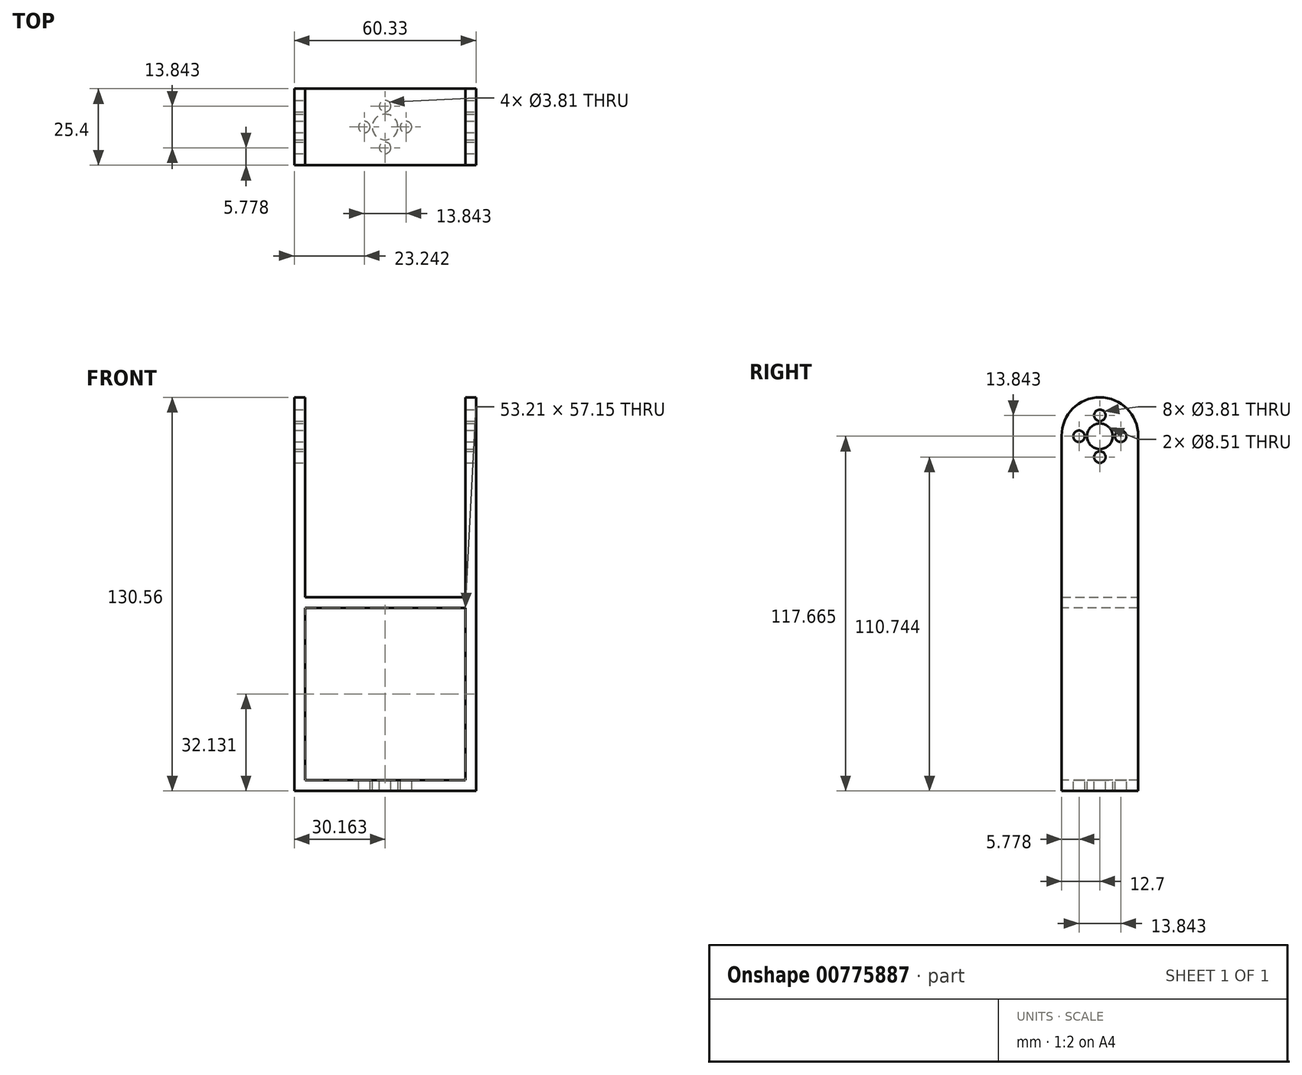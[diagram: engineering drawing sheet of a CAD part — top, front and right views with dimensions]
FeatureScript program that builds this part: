
annotation { "Feature Type Name" : "Feature", "Feature Type Description" : "" }
export const myFeature = defineFeature(function(context is Context, id is Id, definition is map)
    precondition{}
    {
        {
            var Q0;
            Q0=qCreatedBy(makeId("Top.planeOp"),FACE);
            var sketch = newSketch(context, id + "F0", { "sketchPlane" : qUnion([Q0])});
            skLineSegment(sketch, "E0.bottom", {"start": v(-26.29, 12.7) * mm, "end": v(34.04, 12.7) * mm});
            skLineSegment(sketch, "E0.top", {"start": v(-26.29, -12.7) * mm, "end": v(34.04, -12.7) * mm});
            skLineSegment(sketch, "E0.left", {"start": v(-26.29, 12.7) * mm, "end": v(-26.29, -12.7) * mm});
            skLineSegment(sketch, "E0.right", {"start": v(34.04, 12.7) * mm, "end": v(34.04, -12.7) * mm});
            skSolve(sketch);
        }
        {
            var Q0;
            Q0=makeQuery(id+"F0.imprint","IMPRINT",FACE,{"disambiguationData":[TD([[makeQuery(id+"F0.imprint","IMPRINT",EDGE,{"derivedFrom":sQuery(id+"F0.wireOp",EDGE,"E0.bottom")}),-1.0]])]});
            extrude(context, id + "F1", {"entities" : qUnion([Q0]), "depth" : 3.56 * mm});
        }
        {
            var Q0;
            Q0=makeQuery(id+"F1.opExtrude","CAP_FACE",FACE,{"disambiguationData":[OSD([sQuery(id+"F0.wireOp",EDGE,"E0.bottom"),sQuery(id+"F0.wireOp",EDGE,"E0.top"),sQuery(id+"F0.wireOp",EDGE,"E0.left"),sQuery(id+"F0.wireOp",EDGE,"E0.right")])],"isStart":false});
            var sketch = newSketch(context, id + "F2", { "sketchPlane" : qUnion([Q0])});
            skLineSegment(sketch, "E1.bottom", {"start": v(-26.29, 12.7) * mm, "end": v(-22.73, 12.7) * mm});
            skLineSegment(sketch, "E1.top", {"start": v(-26.29, -12.7) * mm, "end": v(-22.73, -12.7) * mm});
            skLineSegment(sketch, "E1.left", {"start": v(-26.29, 12.7) * mm, "end": v(-26.29, -12.7) * mm});
            skLineSegment(sketch, "E1.right", {"start": v(-22.73, 12.7) * mm, "end": v(-22.73, -12.7) * mm});
            skLineSegment(sketch, "E2.bottom", {"start": v(34.04, 12.7) * mm, "end": v(30.48, 12.7) * mm});
            skLineSegment(sketch, "E2.top", {"start": v(34.04, -12.7) * mm, "end": v(30.48, -12.7) * mm});
            skLineSegment(sketch, "E2.left", {"start": v(34.04, 12.7) * mm, "end": v(34.04, -12.7) * mm});
            skLineSegment(sketch, "E2.right", {"start": v(30.48, 12.7) * mm, "end": v(30.48, -12.7) * mm});
            skSolve(sketch);
        }
        {
            var Q0;
            Q0=makeQuery(id+"F2.imprint","IMPRINT",FACE,{"disambiguationData":[TD([[makeQuery(id+"F2.imprint","IMPRINT",EDGE,{"derivedFrom":sQuery(id+"F2.wireOp",EDGE,"E1.bottom")}),-1.0]])]});
            var Q1;
            Q1=makeQuery(id+"F2.imprint","IMPRINT",FACE,{"disambiguationData":[TD([[makeQuery(id+"F2.imprint","IMPRINT",EDGE,{"derivedFrom":sQuery(id+"F2.wireOp",EDGE,"E2.bottom")}),-1.0]])]});
            extrude(context, id + "F3", {"entities" : qUnion([Q0, Q1]), "operationType" : NewBodyOperationType.ADD, "depth" : 127 * mm});
        }
        {
            var Q0;
            Q0=makeQuery(id+"F3.opExtrude","CAP_EDGE",EDGE,{"disambiguationData":[OSD([sQuery(id+"F2.wireOp",EDGE,"E2.bottom")])],"isStart":false});
            fillet(context, id + "F4", {"entities" : qUnion([Q0]), "radius" : 12.7 * mm, "tangentPropagation" : true, "allowEdgeOverflow" : false});
        }
        {
            var Q0;
            Q0=makeQuery(id+"F3.opExtrude","CAP_EDGE",EDGE,{"disambiguationData":[OSD([sQuery(id+"F2.wireOp",EDGE,"E2.top")])],"isStart":false});
            var Q1;
            Q1=makeQuery(id+"F3.opExtrude","CAP_EDGE",EDGE,{"disambiguationData":[OSD([sQuery(id+"F2.wireOp",EDGE,"E1.top")])],"isStart":false});
            var Q2;
            Q2=makeQuery(id+"F3.opExtrude","CAP_EDGE",EDGE,{"disambiguationData":[OSD([sQuery(id+"F2.wireOp",EDGE,"E1.bottom")])],"isStart":false});
            fillet(context, id + "F5", {"entities" : qUnion([Q0, Q1, Q2]), "radius" : 12.7 * mm, "tangentPropagation" : true, "allowEdgeOverflow" : false});
        }
        {
            var Q0;
            Q0=makeQuery(id+"F3.boolean.opBoolean","MERGE",FACE,{"derivedFrom":[makeQuery(id+"F1.opExtrude","SWEPT_FACE",FACE,{"disambiguationData":[OSD([sQuery(id+"F0.wireOp",EDGE,"E0.right")])]}),makeQuery(id+"F3.opExtrude","SWEPT_FACE",FACE,{"disambiguationData":[OSD([sQuery(id+"F2.wireOp",EDGE,"E2.left")])]})]});
            var sketch = newSketch(context, id + "F6", { "sketchPlane" : qUnion([Q0])});
            skCircle(sketch, "E3", {"center": v(0, 124.59) * mm, "radius": 1.9 * mm});
            skCircle(sketch, "E4", {"center": v(0, 110.74) * mm, "radius": 1.9 * mm});
            skCircle(sketch, "E5", {"center": v(0, 117.67) * mm, "radius": 4.25 * mm});
            skCircle(sketch, "E6", {"center": v(6.92, 117.67) * mm, "radius": 1.9 * mm});
            skCircle(sketch, "E7", {"center": v(-6.92, 117.67) * mm, "radius": 1.9 * mm});
            skSolve(sketch);
        }
        {
            var Q0;
            Q0=makeQuery(id+"F6.imprint","IMPRINT",FACE,{"disambiguationData":[TD([[makeQuery(id+"F6.imprint","IMPRINT",EDGE,{"derivedFrom":sQuery(id+"F6.wireOp",EDGE,"E5")}),1.0]])]});
            var Q1;
            Q1=makeQuery(id+"F6.imprint","IMPRINT",FACE,{"disambiguationData":[TD([[makeQuery(id+"F6.imprint","IMPRINT",EDGE,{"derivedFrom":sQuery(id+"F6.wireOp",EDGE,"E3")}),1.0]])]});
            var Q2;
            Q2=makeQuery(id+"F6.imprint","IMPRINT",FACE,{"disambiguationData":[TD([[makeQuery(id+"F6.imprint","IMPRINT",EDGE,{"derivedFrom":sQuery(id+"F6.wireOp",EDGE,"E7")}),1.0]])]});
            var Q3;
            Q3=makeQuery(id+"F6.imprint","IMPRINT",FACE,{"disambiguationData":[TD([[makeQuery(id+"F6.imprint","IMPRINT",EDGE,{"derivedFrom":sQuery(id+"F6.wireOp",EDGE,"E4")}),1.0]])]});
            var Q4;
            Q4=makeQuery(id+"F6.imprint","IMPRINT",FACE,{"disambiguationData":[TD([[makeQuery(id+"F6.imprint","IMPRINT",EDGE,{"derivedFrom":sQuery(id+"F6.wireOp",EDGE,"E6")}),1.0]])]});
            extrude(context, id + "F7", {"entities" : qUnion([Q0, Q1, Q2, Q3, Q4]), "operationType" : NewBodyOperationType.REMOVE, "oppositeDirection" : true, "depth" : 254 * mm});
        }
        {
            var Q0;
            Q0=makeQuery(id+"F1.opExtrude","CAP_FACE",FACE,{"disambiguationData":[OSD([sQuery(id+"F0.wireOp",EDGE,"E0.bottom"),sQuery(id+"F0.wireOp",EDGE,"E0.top"),sQuery(id+"F0.wireOp",EDGE,"E0.left"),sQuery(id+"F0.wireOp",EDGE,"E0.right")])],"isStart":false});
            var sketch = newSketch(context, id + "F8", { "sketchPlane" : qUnion([Q0])});
            skCircle(sketch, "E8", {"center": v(3.87, 0) * mm, "radius": 4.25 * mm});
            skCircle(sketch, "E9", {"center": v(3.87, 6.92) * mm, "radius": 1.9 * mm});
            skCircle(sketch, "E10", {"center": v(10.8, 0) * mm, "radius": 1.9 * mm});
            skCircle(sketch, "E11", {"center": v(3.87, -6.92) * mm, "radius": 1.9 * mm});
            skCircle(sketch, "E12", {"center": v(-3.05, 0) * mm, "radius": 1.9 * mm});
            skSolve(sketch);
        }
        {
            var Q0;
            Q0=makeQuery(id+"F8.imprint","IMPRINT",FACE,{"disambiguationData":[TD([[makeQuery(id+"F8.imprint","IMPRINT",EDGE,{"derivedFrom":sQuery(id+"F8.wireOp",EDGE,"E8")}),1.0]])]});
            var Q1;
            Q1=makeQuery(id+"F8.imprint","IMPRINT",FACE,{"disambiguationData":[TD([[makeQuery(id+"F8.imprint","IMPRINT",EDGE,{"derivedFrom":sQuery(id+"F8.wireOp",EDGE,"E12")}),1.0]])]});
            var Q2;
            Q2=makeQuery(id+"F8.imprint","IMPRINT",FACE,{"disambiguationData":[TD([[makeQuery(id+"F8.imprint","IMPRINT",EDGE,{"derivedFrom":sQuery(id+"F8.wireOp",EDGE,"E9")}),1.0]])]});
            var Q3;
            Q3=makeQuery(id+"F8.imprint","IMPRINT",FACE,{"disambiguationData":[TD([[makeQuery(id+"F8.imprint","IMPRINT",EDGE,{"derivedFrom":sQuery(id+"F8.wireOp",EDGE,"E11")}),1.0]])]});
            var Q4;
            Q4=makeQuery(id+"F8.imprint","IMPRINT",FACE,{"disambiguationData":[TD([[makeQuery(id+"F8.imprint","IMPRINT",EDGE,{"derivedFrom":sQuery(id+"F8.wireOp",EDGE,"E10")}),1.0]])]});
            extrude(context, id + "F9", {"entities" : qUnion([Q0, Q1, Q2, Q3, Q4]), "operationType" : NewBodyOperationType.REMOVE, "oppositeDirection" : true, "depth" : 25.4 * mm});
        }
        {
            var Q0;
            Q0=makeQuery(id+"F3.opExtrude","SWEPT_FACE",FACE,{"disambiguationData":[OSD([sQuery(id+"F2.wireOp",EDGE,"E1.right")])]});
            var sketch = newSketch(context, id + "F10", { "sketchPlane" : qUnion([Q0])});
            skLineSegment(sketch, "E13.bottom", {"start": v(12.7, 64.26) * mm, "end": v(-12.7, 64.26) * mm});
            skLineSegment(sketch, "E13.top", {"start": v(12.7, 60.7) * mm, "end": v(-12.7, 60.7) * mm});
            skLineSegment(sketch, "E13.left", {"start": v(12.7, 64.26) * mm, "end": v(12.7, 60.7) * mm});
            skLineSegment(sketch, "E13.right", {"start": v(-12.7, 64.26) * mm, "end": v(-12.7, 60.7) * mm});
            skSolve(sketch);
        }
        {
            var Q0;
            Q0=makeQuery(id+"F10.imprint","IMPRINT",FACE,{"disambiguationData":[TD([[makeQuery(id+"F10.imprint","IMPRINT",EDGE,{"derivedFrom":sQuery(id+"F10.wireOp",EDGE,"E13.bottom")}),1.0]])]});
            extrude(context, id + "F11", {"entities" : qUnion([Q0]), "operationType" : NewBodyOperationType.ADD, "depth" : 53.34 * mm});
        }
    });
